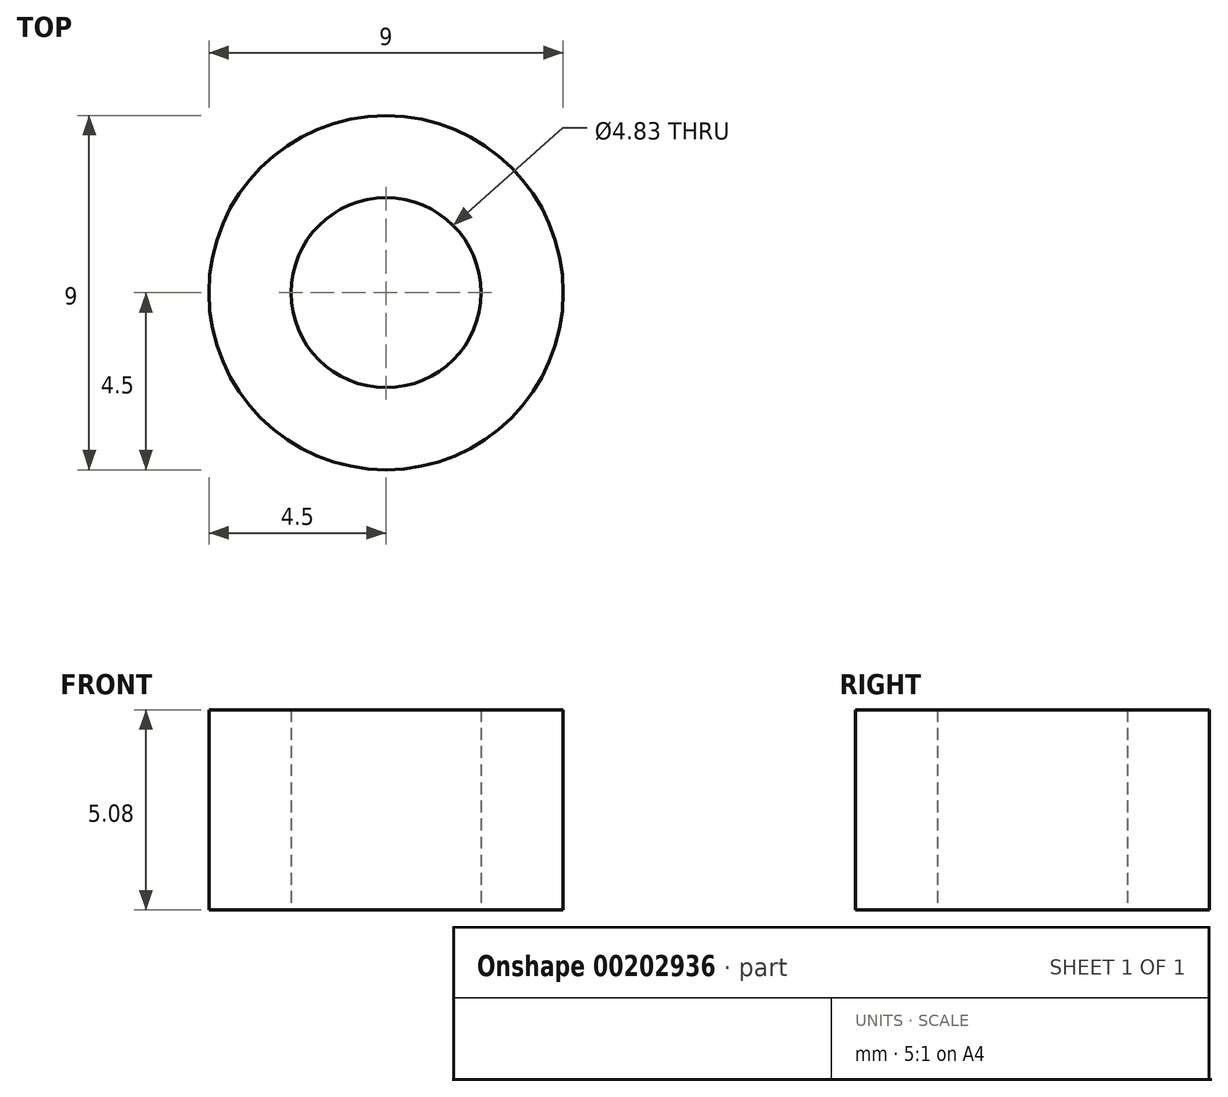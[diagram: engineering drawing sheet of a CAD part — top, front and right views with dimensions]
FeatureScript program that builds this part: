
annotation { "Feature Type Name" : "Feature", "Feature Type Description" : "" }
export const myFeature = defineFeature(function(context is Context, id is Id, definition is map)
    precondition{}
    {
        {
            var Q0;
            Q0=qCreatedBy(makeId("Top.planeOp"),FACE);
            var sketch = newSketch(context, id + "F0", { "sketchPlane" : qUnion([Q0])});
            skCircle(sketch, "E0", {"center": v(0, 0) * mm, "radius": 4.5 * mm});
            skCircle(sketch, "E1", {"center": v(0, 0) * mm, "radius": 2.41 * mm});
            skSolve(sketch);
        }
        {
            var Q0;
            Q0 = qSketchRegion(id + "F0", true);
            extrude(context, id + "F1", {"entities" : qUnion([Q0]), "depth" : 5.08 * mm});
        }
    });
